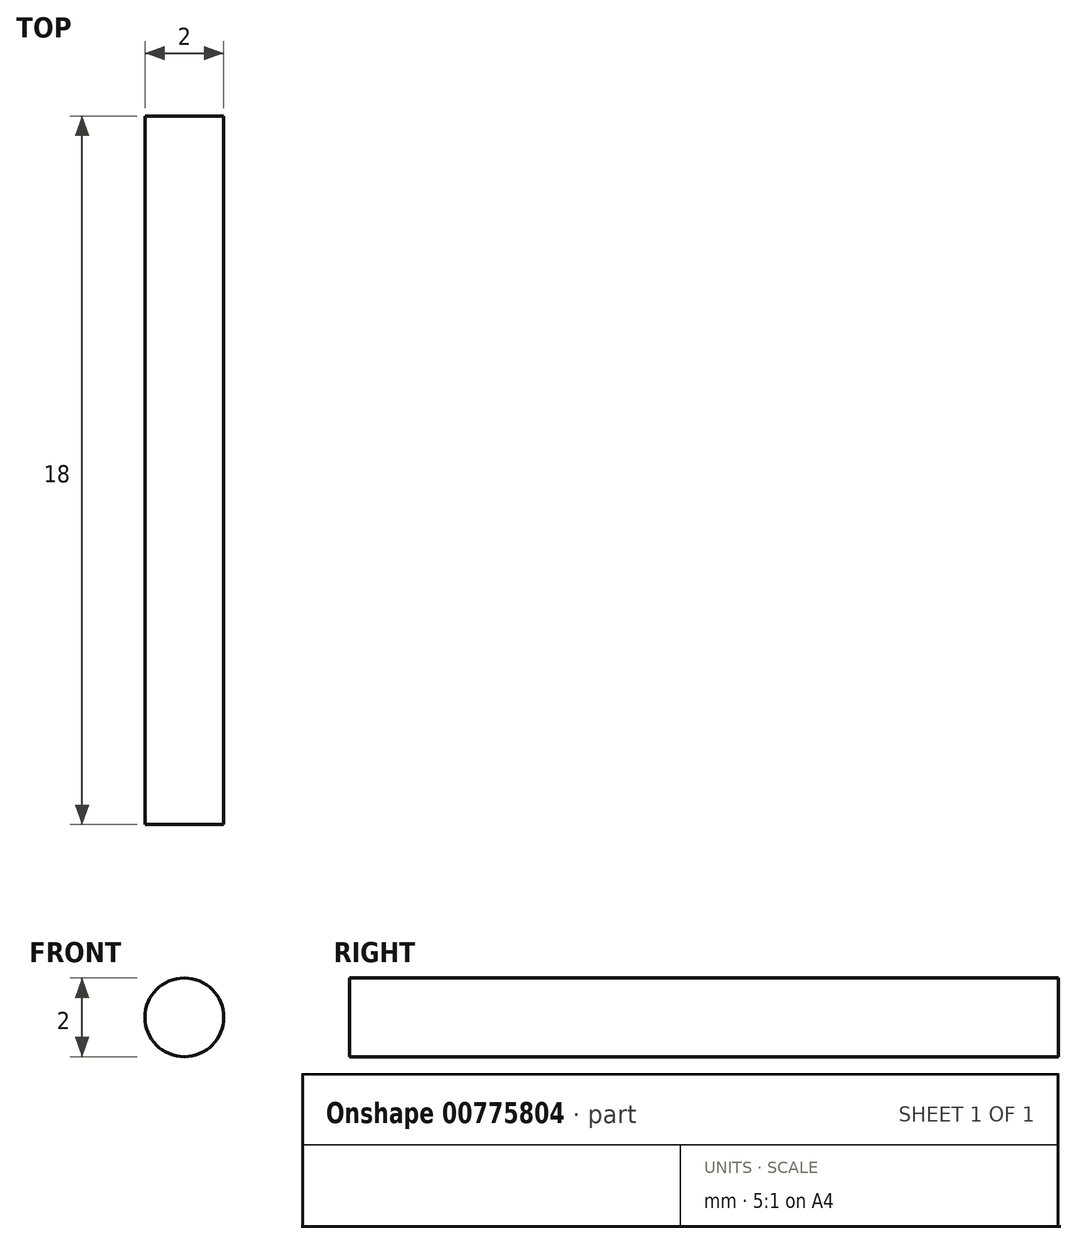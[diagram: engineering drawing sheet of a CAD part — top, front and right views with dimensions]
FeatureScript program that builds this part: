
annotation { "Feature Type Name" : "Feature", "Feature Type Description" : "" }
export const myFeature = defineFeature(function(context is Context, id is Id, definition is map)
    precondition{}
    {
        {
            var Q0;
            Q0=qCreatedBy(makeId("Front.planeOp"),FACE);
            var sketch = newSketch(context, id + "F0", { "sketchPlane" : qUnion([Q0])});
            skCircle(sketch, "E0", {"center": v(0, 0) * mm, "radius": 1 * mm});
            skSolve(sketch);
        }
        {
            var Q0;
            Q0=makeQuery(id+"F0.imprint","IMPRINT",FACE,{"disambiguationData":[TD([[makeQuery(id+"F0.imprint","IMPRINT",EDGE,{"derivedFrom":sQuery(id+"F0.wireOp",EDGE,"E0")}),1.0]])]});
            extrude(context, id + "F1", {"entities" : qUnion([Q0]), "endBound" : BoundingType.SYMMETRIC, "depth" : 18 * mm, "offsetDistance" : 25 * mm});
        }
    });
